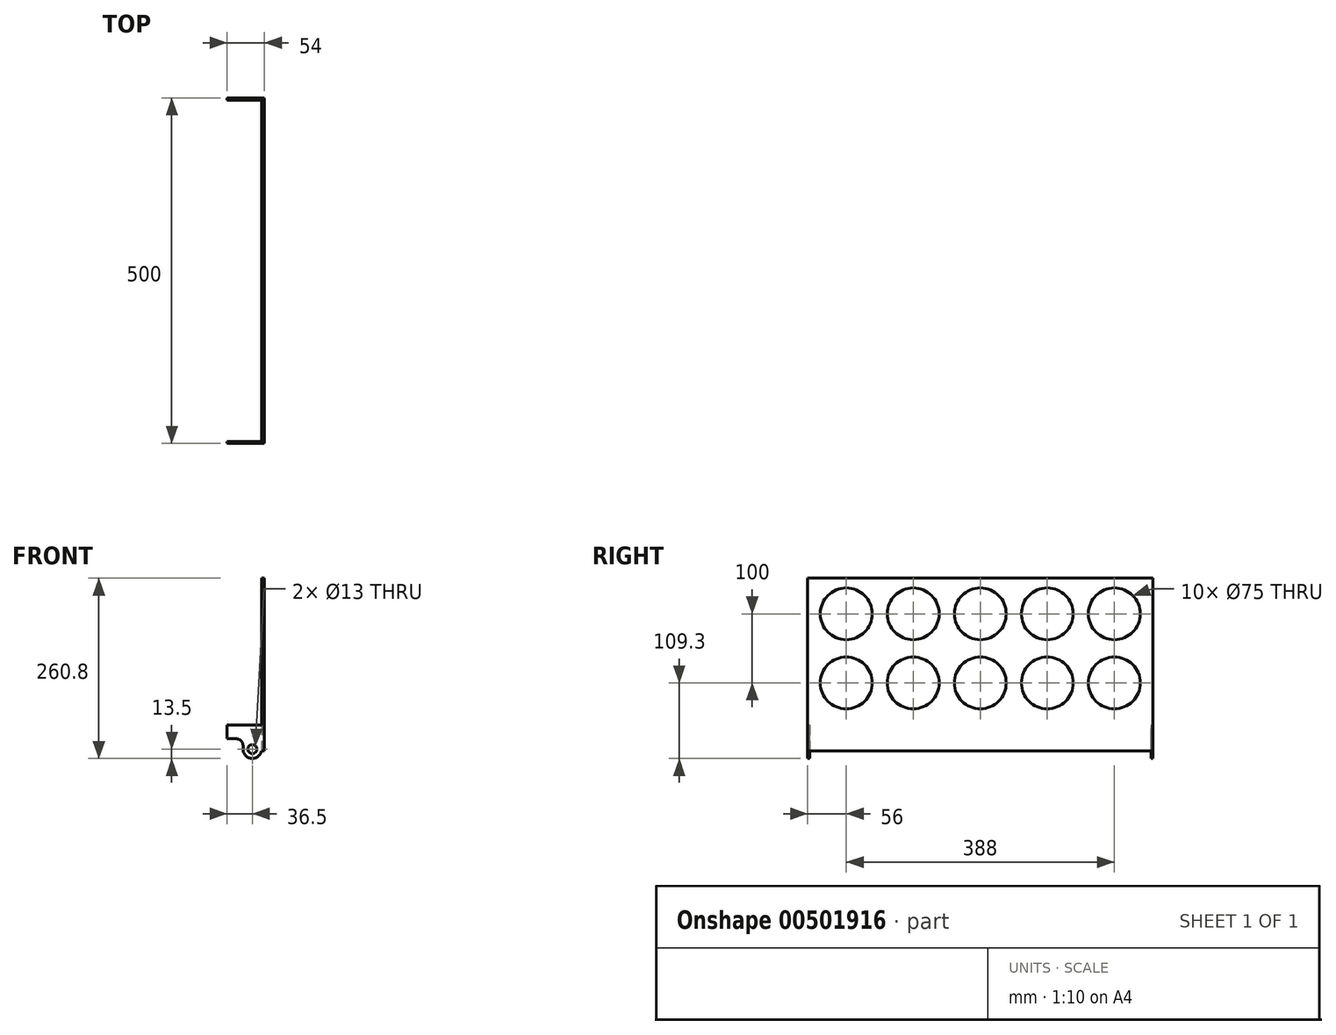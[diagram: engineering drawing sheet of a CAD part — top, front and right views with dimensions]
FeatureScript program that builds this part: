
annotation { "Feature Type Name" : "Feature", "Feature Type Description" : "" }
export const myFeature = defineFeature(function(context is Context, id is Id, definition is map)
    precondition{}
    {
        {
            var Q0;
            Q0=qCreatedBy(makeId("Front.planeOp"),FACE);
            var sketch = newSketch(context, id + "F0", { "sketchPlane" : qUnion([Q0])});
            skArc(sketch, "E0", {"start": v(-13.5, 0) * mm, "mid": v(-1.36, -13.43) * mm, "end": v(13.23, -2.7) * mm});
            skLineSegment(sketch, "E1.left", {"start": v(-13.5, 0) * mm, "end": v(-13.5, 15) * mm});
            skLineSegment(sketch, "E1.right", {"start": v(13.5, -2.7) * mm, "end": v(13.5, 15) * mm});
            skLineSegment(sketch, "E2.trimOffspring", {"start": v(13.23, -2.7) * mm, "end": v(13.5, -2.7) * mm});
            skLineSegment(sketch, "E3.bottom", {"start": v(-13.5, 15) * mm, "end": v(-36.5, 15) * mm});
            skLineSegment(sketch, "E3.top", {"start": v(13.5, 35) * mm, "end": v(-36.5, 35) * mm});
            skLineSegment(sketch, "E3.left", {"start": v(13.5, 15) * mm, "end": v(13.5, 35) * mm});
            skLineSegment(sketch, "E3.right", {"start": v(-36.5, 15) * mm, "end": v(-36.5, 35) * mm});
            skPoint(sketch, "E4.start.orphan", {"position": v(-6.5, 0) * mm});
            skPoint(sketch, "E5.end.orphan", {"position": v(6.5, 0) * mm});
            skCircle(sketch, "E6", {"center": v(0, 0) * mm, "radius": 6.5 * mm});
            skSolve(sketch);
        }
        {
            var Q0;
            Q0=makeQuery(id+"F0.imprint","IMPRINT",FACE,{"disambiguationData":[TD([[makeQuery(id+"F0.imprint","IMPRINT",EDGE,{"derivedFrom":sQuery(id+"F0.wireOp",EDGE,"E0")}),1.0]])]});
            extrude(context, id + "F1", {"entities" : qUnion([Q0]), "endBound" : BoundingType.SYMMETRIC, "depth" : 500 * mm});
        }
        {
            var Q0;
            Q0=makeQuery(id+"F1.opExtrude","SWEPT_FACE",FACE,{"disambiguationData":[OSD([sQuery(id+"F0.wireOp",EDGE,"E1.right"),sQuery(id+"F0.wireOp",EDGE,"E3.left")])]});
            var sketch = newSketch(context, id + "F2", { "sketchPlane" : qUnion([Q0])});
            skLineSegment(sketch, "E7.bottom", {"start": v(-247, 50) * mm, "end": v(247, 50) * mm});
            skLineSegment(sketch, "E7.top", {"start": v(-247, -50) * mm, "end": v(247, -50) * mm});
            skLineSegment(sketch, "E7.left", {"start": v(-247, 50) * mm, "end": v(-247, -50) * mm});
            skLineSegment(sketch, "E7.right", {"start": v(247, 50) * mm, "end": v(247, -50) * mm});
            skPoint(sketch, "E7.middle", {"position": v(0, 0) * mm});
            skSolve(sketch);
        }
        {
            var Q0;
            Q0 = qSketchRegion(id + "F2", true);
            extrude(context, id + "F3", {"entities" : qUnion([Q0]), "operationType" : NewBodyOperationType.REMOVE, "oppositeDirection" : true, "depth" : 100 * mm});
        }
        {
            var Q0;
            {var subQ0=sQuery(id+"F0.wireOp",EDGE,"E3.bottom");var subQ1=sQuery(id+"F0.wireOp",EDGE,"E1.left");Q0=makeQuery(id+"F3.boolean.opBoolean","SPLIT",EDGE,{"disambiguationData":[TD([makeQuery(id+"F3.opExtrude","SWEPT_FACE",FACE,{"disambiguationData":[OSD([sQuery(id+"F2.wireOp",EDGE,"E7.left")])]})])],"derivedFrom":makeQuery(id+"F1.opExtrude","SWEPT_EDGE",EDGE,{"disambiguationData":[OSD([subQ1,subQ0])]})});}
            var Q1;
            {var subQ0=sQuery(id+"F0.wireOp",EDGE,"E3.bottom");var subQ1=sQuery(id+"F0.wireOp",EDGE,"E1.left");Q1=makeQuery(id+"F3.boolean.opBoolean","SPLIT",EDGE,{"disambiguationData":[TD([makeQuery(id+"F3.opExtrude","SWEPT_FACE",FACE,{"disambiguationData":[OSD([sQuery(id+"F2.wireOp",EDGE,"E7.right")])]})])],"derivedFrom":makeQuery(id+"F1.opExtrude","SWEPT_EDGE",EDGE,{"disambiguationData":[OSD([subQ1,subQ0])]})});}
            fillet(context, id + "F4", {"entities" : qUnion([Q0, Q1]), "radius" : 10 * mm, "tangentPropagation" : true, "allowEdgeOverflow" : false});
        }
        {
            var Q0;
            {var subQ0=sQuery(id+"F0.wireOp",EDGE,"E3.left");var subQ3=sQuery(id+"F0.wireOp",EDGE,"E1.right");Q0=makeQuery(id+"F3.boolean.opBoolean","SPLIT",FACE,{"disambiguationData":[TD([makeQuery(id+"F3.opExtrude","SWEPT_FACE",FACE,{"disambiguationData":[OSD([sQuery(id+"F2.wireOp",EDGE,"E7.left")])]})])],"derivedFrom":makeQuery(id+"F1.opExtrude","SWEPT_FACE",FACE,{"disambiguationData":[OSD([subQ3,subQ0])]})});}
            var sketch = newSketch(context, id + "F5", { "sketchPlane" : qUnion([Q0])});
            skLineSegment(sketch, "E8.bottom", {"start": v(-250, -2.7) * mm, "end": v(250, -2.7) * mm});
            skLineSegment(sketch, "E8.top", {"start": v(-250, 247.3) * mm, "end": v(250, 247.3) * mm});
            skLineSegment(sketch, "E8.left", {"start": v(-250, -2.7) * mm, "end": v(-250, 247.3) * mm});
            skLineSegment(sketch, "E8.right", {"start": v(250, -2.7) * mm, "end": v(250, 247.3) * mm});
            skSolve(sketch);
        }
        {
            var Q0;
            Q0 = qSketchRegion(id + "F5", true);
            extrude(context, id + "F6", {"entities" : qUnion([Q0]), "operationType" : NewBodyOperationType.ADD, "depth" : 4 * mm});
        }
        {
            var Q0;
            Q0=makeQuery(id+"F6.opExtrude","CAP_FACE",FACE,{"disambiguationData":[OSD([sQuery(id+"F5.wireOp",EDGE,"E8.bottom"),sQuery(id+"F5.wireOp",EDGE,"E8.top"),sQuery(id+"F5.wireOp",EDGE,"E8.left"),sQuery(id+"F5.wireOp",EDGE,"E8.right")])],"isStart":false});
            var sketch = newSketch(context, id + "F7", { "sketchPlane" : qUnion([Q0])});
            skCircle(sketch, "E9", {"center": v(-194, 95.8) * mm, "radius": 37.5 * mm});
            skCircle(sketch, "E10", {"center": v(-194, 195.8) * mm, "radius": 37.5 * mm});
            skCircle(sketch, "E11.1.0.0", {"center": v(-97, 95.8) * mm, "radius": 37.5 * mm});
            skCircle(sketch, "E11.1.0.1", {"center": v(-97, 195.8) * mm, "radius": 37.5 * mm});
            skCircle(sketch, "E11.2.0.0", {"center": v(0, 95.8) * mm, "radius": 37.5 * mm});
            skCircle(sketch, "E11.2.0.1", {"center": v(0, 195.8) * mm, "radius": 37.5 * mm});
            skCircle(sketch, "E11.3.0.0", {"center": v(97, 95.8) * mm, "radius": 37.5 * mm});
            skCircle(sketch, "E11.3.0.1", {"center": v(97, 195.8) * mm, "radius": 37.5 * mm});
            skCircle(sketch, "E11.4.0.0", {"center": v(194, 95.8) * mm, "radius": 37.5 * mm});
            skCircle(sketch, "E11.4.0.1", {"center": v(194, 195.8) * mm, "radius": 37.5 * mm});
            skLineSegment(sketch, "E11.direction1", {"start": v(-194, 95.8) * mm, "end": v(-97, 95.8) * mm, "construction": true});
            skSolve(sketch);
        }
        {
            var Q0;
            Q0 = qSketchRegion(id + "F7", true);
            extrude(context, id + "F8", {"entities" : qUnion([Q0]), "operationType" : NewBodyOperationType.REMOVE, "oppositeDirection" : true, "depth" : 25 * mm});
        }
    });
